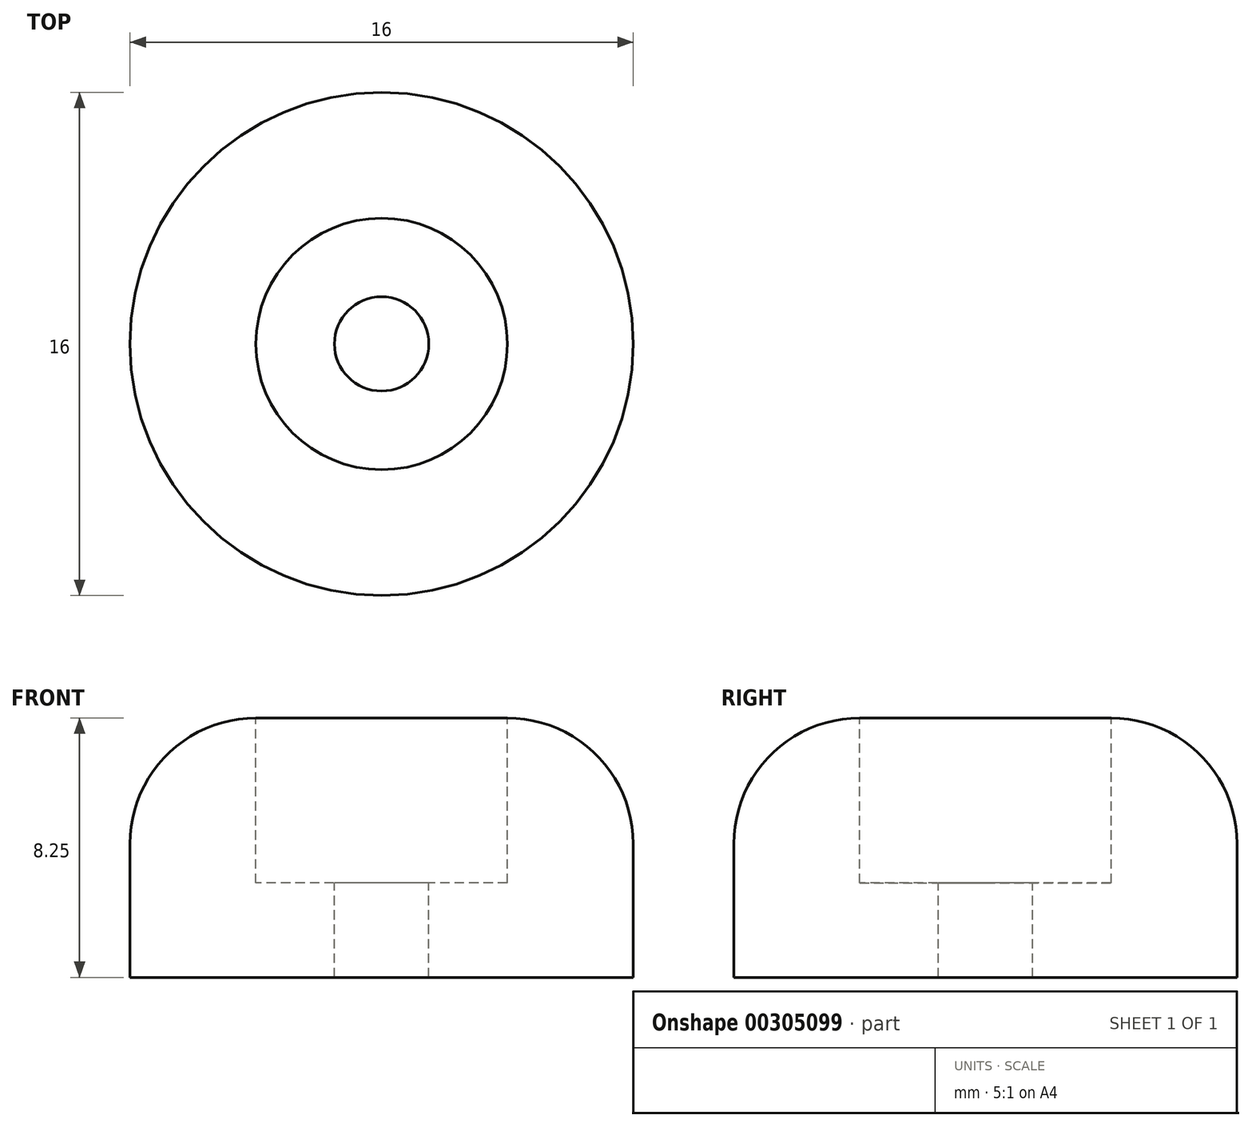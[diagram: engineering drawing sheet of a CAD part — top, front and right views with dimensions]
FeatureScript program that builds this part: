
annotation { "Feature Type Name" : "Feature", "Feature Type Description" : "" }
export const myFeature = defineFeature(function(context is Context, id is Id, definition is map)
    precondition{}
    {
        {
            var Q0;
            Q0=qCreatedBy(makeId("Front.planeOp"),FACE);
            var sketch = newSketch(context, id + "F0", { "sketchPlane" : qUnion([Q0])});
            skLineSegment(sketch, "E0", {"start": v(0, 0) * mm, "end": v(-4, 0) * mm});
            skLineSegment(sketch, "E1", {"start": v(-4, 0) * mm, "end": v(-4, 5.25) * mm});
            skLineSegment(sketch, "E2", {"start": v(-4, 5.25) * mm, "end": v(-4, 5.25) * mm});
            skLineSegment(sketch, "E3", {"start": v(-8, 1.25) * mm, "end": v(-8, -3) * mm});
            skLineSegment(sketch, "E4", {"start": v(-8, -3) * mm, "end": v(0, -3) * mm});
            skLineSegment(sketch, "E5", {"start": v(0, -3) * mm, "end": v(0, 0) * mm});
            skCircle(sketch, "E6", {"center": v(0, 0) * mm, "radius": 1.5 * mm, "construction": true});
            skPoint(sketch, "E7.visualSharp", {"position": v(-8, 5.25) * mm});
            skArc(sketch, "E7.filletArc", {"start": v(-4, 5.25) * mm, "mid": v(-6.83, 4.08) * mm, "end": v(-8, 1.25) * mm});
            skLineSegment(sketch, "E8", {"start": v(0, 6.23) * mm, "end": v(0, -16.89) * mm, "construction": true});
            skSolve(sketch);
        }
        {
            var Q0;
            Q0=makeQuery(id+"F0.imprint","IMPRINT",FACE,{"disambiguationData":[TD([[makeQuery(id+"F0.imprint","IMPRINT",EDGE,{"derivedFrom":sQuery(id+"F0.wireOp",EDGE,"E0")}),1.0]])]});
            var Q1;
            Q1=sQuery(id+"F0.wireOp",EDGE,"E8");
            revolve(context, id + "F1", {"entities" : qUnion([Q0]), "axis" : qUnion([Q1]), "revolveType" : RevolveType.FULL});
        }
        {
            var Q0;
            Q0=makeQuery(id+"F1.opRevolve","SWEPT_FACE",FACE,{"disambiguationData":[OSD([sQuery(id+"F0.wireOp",EDGE,"E0")])]});
            var sketch = newSketch(context, id + "F2", { "sketchPlane" : qUnion([Q0])});
            skCircle(sketch, "E9", {"center": v(0, 0) * mm, "radius": 1.5 * mm});
            skSolve(sketch);
        }
        {
            var Q0;
            Q0=makeQuery(id+"F2.imprint","IMPRINT",FACE,{"disambiguationData":[TD([[makeQuery(id+"F2.imprint","IMPRINT",EDGE,{"derivedFrom":sQuery(id+"F2.wireOp",EDGE,"E9")}),1.0]])]});
            var Q1;
            Q1=sQuery(id+"F2.wireOp",EDGE,"E9");
            extrude(context, id + "F3", {"entities" : qUnion([Q0]), "operationType" : NewBodyOperationType.REMOVE, "surfaceEntities" : qUnion([Q1]), "oppositeDirection" : true, "depth" : 10 * mm});
        }
    });
